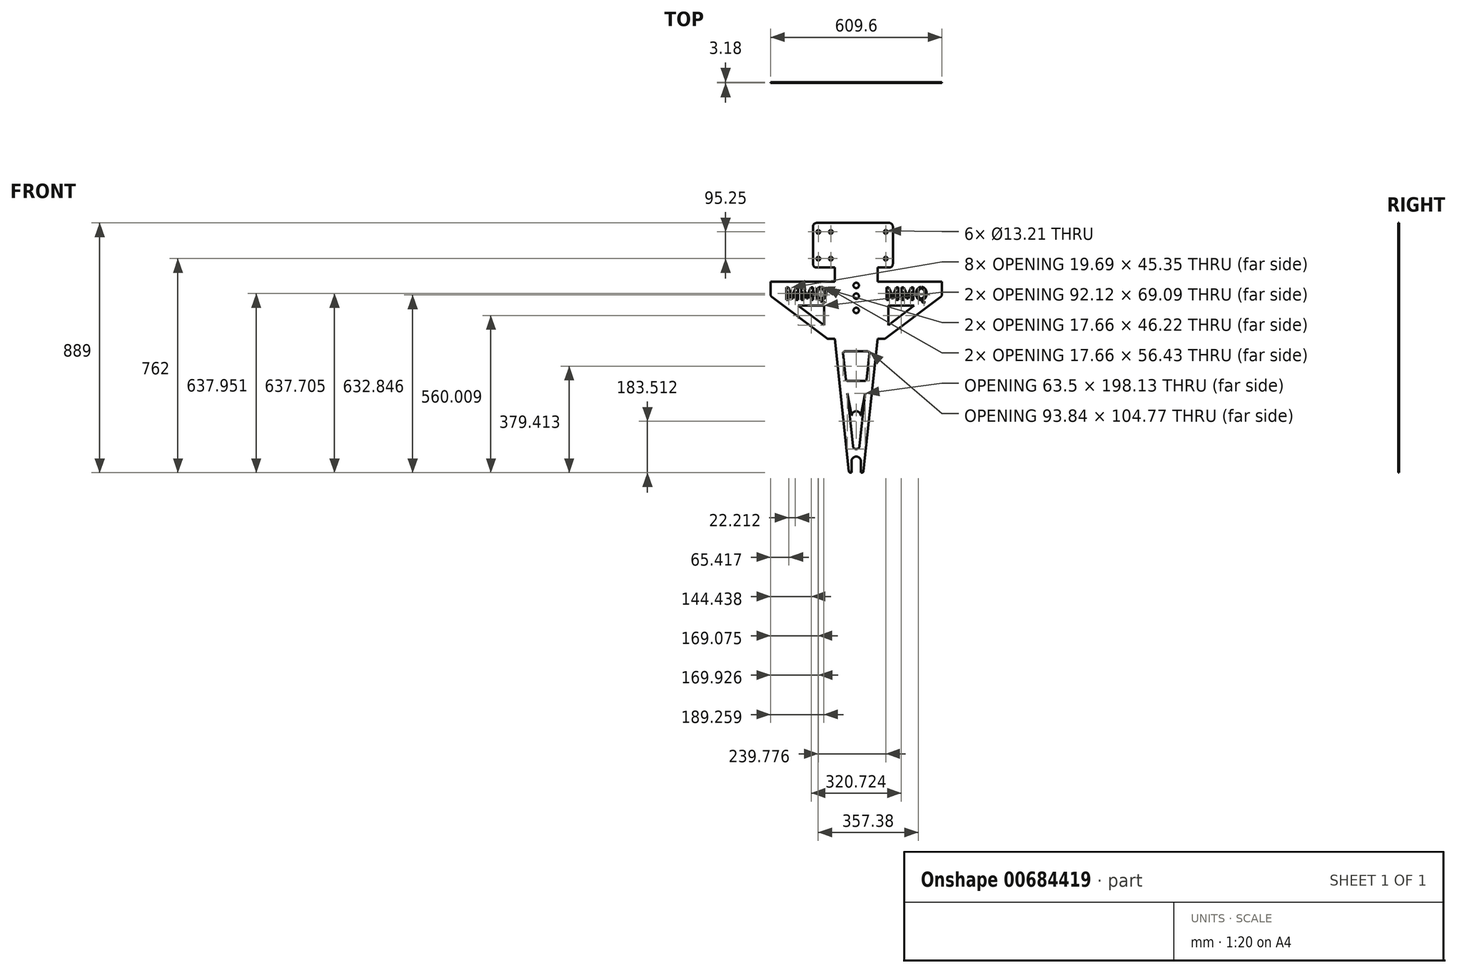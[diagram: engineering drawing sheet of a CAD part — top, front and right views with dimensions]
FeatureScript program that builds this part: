
annotation { "Feature Type Name" : "Feature", "Feature Type Description" : "" }
export const myFeature = defineFeature(function(context is Context, id is Id, definition is map)
    precondition{}
    {
        {
            var Q0;
            Q0=qCreatedBy(makeId("Front.planeOp"),FACE);
            var sketch = newSketch(context, id + "F0", { "sketchPlane" : qUnion([Q0])});
            skLineSegment(sketch, "E0.bottom", {"start": v(-97.37, -101.6) * mm, "end": v(-76.2, -101.6) * mm});
            skLineSegment(sketch, "E0.top", {"start": v(-304.8, 101.6) * mm, "end": v(-76.2, 101.6) * mm});
            skLineSegment(sketch, "E0.left", {"start": v(-304.8, 57.15) * mm, "end": v(-304.8, 101.6) * mm});
            skLineSegment(sketch, "E0.right", {"start": v(304.8, 57.15) * mm, "end": v(304.8, 101.6) * mm});
            skPoint(sketch, "E0.middle", {"position": v(0, 0) * mm});
            skLineSegment(sketch, "E1", {"start": v(-16.52, -577.85) * mm, "end": v(-19.7, -577.85) * mm});
            skLineSegment(sketch, "E2", {"start": v(16.5, -577.85) * mm, "end": v(19.7, -577.85) * mm});
            skPoint(sketch, "E3", {"position": v(-76.2, -101.6) * mm});
            skPoint(sketch, "E4", {"position": v(76.2, -101.6) * mm});
            skLineSegment(sketch, "E5", {"start": v(-76.2, -101.6) * mm, "end": v(-26, -572.17) * mm});
            skLineSegment(sketch, "E6", {"start": v(76.2, -101.6) * mm, "end": v(26, -572.17) * mm});
            skPoint(sketch, "E7", {"position": v(0, -295.28) * mm});
            skPoint(sketch, "E8", {"position": v(0, -523.88) * mm});
            skPoint(sketch, "E9", {"position": v(-31.75, -295.28) * mm});
            skPoint(sketch, "E10", {"position": v(31.75, -295.28) * mm});
            skArc(sketch, "E11", {"start": v(15.88, -374.65) * mm, "mid": v(0, -358.78) * mm, "end": v(-15.87, -374.65) * mm});
            skLineSegment(sketch, "E12", {"start": v(-31.75, -295.28) * mm, "end": v(-16.18, -374.65) * mm});
            skLineSegment(sketch, "E13", {"start": v(31.75, -295.28) * mm, "end": v(16.18, -374.65) * mm});
            skLineSegment(sketch, "E14", {"start": v(-31.75, -295.28) * mm, "end": v(-11.88, -481.52) * mm});
            skLineSegment(sketch, "E15", {"start": v(31.75, -295.28) * mm, "end": v(11.88, -481.52) * mm});
            skArc(sketch, "E16", {"start": v(-11.88, -481.52) * mm, "mid": v(0, -493.4) * mm, "end": v(11.88, -481.52) * mm});
            skLineSegment(sketch, "E17", {"start": v(-76.2, 101.6) * mm, "end": v(-76.2, 152.4) * mm});
            skPoint(sketch, "E17.startSnap0", {"position": v(0, 101.6) * mm});
            skLineSegment(sketch, "E18", {"start": v(76.2, 101.6) * mm, "end": v(76.2, 152.4) * mm});
            skLineSegment(sketch, "E19", {"start": v(-76.2, 152.4) * mm, "end": v(-141.22, 152.4) * mm});
            skLineSegment(sketch, "E20", {"start": v(76.2, 152.4) * mm, "end": v(117.6, 152.4) * mm});
            skPoint(sketch, "E21.orphan", {"position": v(-141.22, 361.95) * mm});
            skPoint(sketch, "E22.orphan", {"position": v(117.6, 361.95) * mm});
            skLineSegment(sketch, "E23", {"start": v(-153.92, 298.45) * mm, "end": v(-153.92, 165.1) * mm});
            skPoint(sketch, "E23.endSnap0", {"position": v(-108.71, 152.4) * mm});
            skLineSegment(sketch, "E24", {"start": v(130.3, 298.45) * mm, "end": v(130.3, 165.1) * mm});
            skLineSegment(sketch, "E25", {"start": v(-141.22, 152.4) * mm, "end": v(-141.22, 152.4) * mm});
            skLineSegment(sketch, "E26", {"start": v(117.6, 152.4) * mm, "end": v(117.6, 152.4) * mm});
            skPoint(sketch, "E27.end.orphan", {"position": v(-141.22, 317.6) * mm});
            skPoint(sketch, "E28.start.orphan", {"position": v(117.6, 317.5) * mm});
            skPoint(sketch, "E29.start.orphan", {"position": v(-15.88, -539.75) * mm});
            skPoint(sketch, "E30.start.orphan", {"position": v(15.87, -539.75) * mm});
            skPoint(sketch, "E31.center.orphan", {"position": v(0, -552.44) * mm});
            skArc(sketch, "E32", {"start": v(16.5, -536.58) * mm, "mid": v(0, -520.07) * mm, "end": v(-16.52, -536.58) * mm});
            skLineSegment(sketch, "E33", {"start": v(16.5, -577.85) * mm, "end": v(16.5, -536.58) * mm});
            skLineSegment(sketch, "E34", {"start": v(-16.52, -577.85) * mm, "end": v(-16.52, -536.58) * mm});
            skPoint(sketch, "E35", {"position": v(0, -520.07) * mm});
            skLineSegment(sketch, "E36", {"start": v(-299.72, 46.99) * mm, "end": v(-104.99, -99.06) * mm});
            skLineSegment(sketch, "E37", {"start": v(299.72, 46.99) * mm, "end": v(104.99, -99.06) * mm});
            skPoint(sketch, "E38.orphan", {"position": v(-304.8, -101.6) * mm});
            skPoint(sketch, "E39.orphan", {"position": v(304.8, -101.6) * mm});
            skLineSegment(sketch, "E40.trimOffspring", {"start": v(76.2, 101.6) * mm, "end": v(304.8, 101.6) * mm});
            skLineSegment(sketch, "E41.trimOffspring", {"start": v(76.2, -101.6) * mm, "end": v(97.37, -101.6) * mm});
            skCircle(sketch, "E42", {"center": v(104.9, 279.4) * mm, "radius": 6.6 * mm});
            skCircle(sketch, "E43", {"center": v(104.9, 184.15) * mm, "radius": 6.6 * mm});
            skCircle(sketch, "E44", {"center": v(-90.42, 184.15) * mm, "radius": 6.6 * mm});
            skCircle(sketch, "E45", {"center": v(-90.42, 279.4) * mm, "radius": 6.6 * mm});
            skPoint(sketch, "E46", {"position": v(0, 184.15) * mm});
            skPoint(sketch, "E47", {"position": v(0, 279.4) * mm});
            skLineSegment(sketch, "E48", {"start": v(-141.22, 311.15) * mm, "end": v(117.6, 311.15) * mm});
            skPoint(sketch, "E49.end.orphan", {"position": v(130.3, 317.5) * mm});
            skPoint(sketch, "E50.orphan", {"position": v(-153.92, 317.6) * mm});
            skLineSegment(sketch, "E51", {"start": v(-115.82, 285.75) * mm, "end": v(-115.82, 177.8) * mm});
            skCircle(sketch, "E52", {"center": v(-134.87, 184.15) * mm, "radius": 6.6 * mm});
            skCircle(sketch, "E53", {"center": v(-134.87, 279.4) * mm, "radius": 6.6 * mm});
            skPoint(sketch, "E54", {"position": v(-115.82, 285.75) * mm});
            skPoint(sketch, "E55", {"position": v(-115.82, 177.8) * mm});
            skPoint(sketch, "E56.orphan", {"position": v(-115.82, 311.15) * mm});
            skPoint(sketch, "E57.orphan", {"position": v(-115.82, 152.4) * mm});
            skPoint(sketch, "E58.orphan", {"position": v(0, -101.6) * mm});
            skPoint(sketch, "E59.trimOffspring.end.orphan", {"position": v(0, -539.75) * mm});
            skCircle(sketch, "E60", {"center": v(0, 50.8) * mm, "radius": 9.78 * mm});
            skText(sketch, "E61", { "text": "MMQ", "fontName": "AllertaStencil-Regular.ttf"});
            skPoint(sketch, "E62.visualSharp", {"position": v(-153.92, 311.15) * mm});
            skArc(sketch, "E62.filletArc", {"start": v(-141.22, 311.15) * mm, "mid": v(-150.2, 307.43) * mm, "end": v(-153.92, 298.45) * mm});
            skPoint(sketch, "E63.visualSharp", {"position": v(-153.92, 152.4) * mm});
            skArc(sketch, "E63.filletArc", {"start": v(-153.92, 165.1) * mm, "mid": v(-150.2, 156.12) * mm, "end": v(-141.22, 152.4) * mm});
            skPoint(sketch, "E64.visualSharp", {"position": v(130.3, 311.15) * mm});
            skArc(sketch, "E64.filletArc", {"start": v(130.3, 298.45) * mm, "mid": v(126.58, 307.43) * mm, "end": v(117.6, 311.15) * mm});
            skPoint(sketch, "E65.visualSharp", {"position": v(130.3, 152.4) * mm});
            skArc(sketch, "E65.filletArc", {"start": v(117.6, 152.4) * mm, "mid": v(126.58, 156.12) * mm, "end": v(130.3, 165.1) * mm});
            skPoint(sketch, "E66.visualSharp", {"position": v(-304.8, 50.8) * mm});
            skArc(sketch, "E66.filletArc", {"start": v(-304.8, 57.15) * mm, "mid": v(-303.46, 51.47) * mm, "end": v(-299.72, 46.99) * mm});
            skPoint(sketch, "E67.visualSharp", {"position": v(-101.6, -101.6) * mm});
            skArc(sketch, "E67.filletArc", {"start": v(-104.99, -99.06) * mm, "mid": v(-101.38, -100.95) * mm, "end": v(-97.37, -101.6) * mm});
            skPoint(sketch, "E68.visualSharp", {"position": v(101.6, -101.6) * mm});
            skArc(sketch, "E68.filletArc", {"start": v(97.37, -101.6) * mm, "mid": v(101.38, -100.95) * mm, "end": v(104.99, -99.06) * mm});
            skPoint(sketch, "E69.visualSharp", {"position": v(304.8, 50.8) * mm});
            skArc(sketch, "E69.filletArc", {"start": v(299.72, 46.99) * mm, "mid": v(303.46, 51.47) * mm, "end": v(304.8, 57.15) * mm});
            skPoint(sketch, "E70.visualSharp", {"position": v(-25.4, -577.85) * mm});
            skArc(sketch, "E70.filletArc", {"start": v(-26, -572.17) * mm, "mid": v(-23.94, -576.22) * mm, "end": v(-19.7, -577.85) * mm});
            skPoint(sketch, "E71.visualSharp", {"position": v(25.4, -577.85) * mm});
            skArc(sketch, "E71.filletArc", {"start": v(19.7, -577.85) * mm, "mid": v(23.94, -576.22) * mm, "end": v(26, -572.17) * mm});
            skLineSegment(sketch, "E72", {"start": v(-37.1, -245.15) * mm, "end": v(-46.92, -153.07) * mm});
            skLineSegment(sketch, "E73", {"start": v(37.1, -245.15) * mm, "end": v(46.92, -153.07) * mm});
            skLineSegment(sketch, "E74", {"start": v(15.2, -146.05) * mm, "end": v(-15.2, -146.05) * mm});
            skLineSegment(sketch, "E75", {"start": v(-30.78, -250.83) * mm, "end": v(30.78, -250.83) * mm});
            skPoint(sketch, "E76.visualSharp", {"position": v(-47.67, -146.05) * mm});
            skArc(sketch, "E76.filletArc", {"start": v(-40.6, -146.05) * mm, "mid": v(-45.33, -148.15) * mm, "end": v(-46.92, -153.07) * mm});
            skPoint(sketch, "E77.visualSharp", {"position": v(47.67, -146.05) * mm});
            skArc(sketch, "E77.filletArc", {"start": v(46.92, -153.07) * mm, "mid": v(45.33, -148.15) * mm, "end": v(40.6, -146.05) * mm});
            skPoint(sketch, "E78.visualSharp", {"position": v(36.5, -250.83) * mm});
            skArc(sketch, "E78.filletArc", {"start": v(30.78, -250.83) * mm, "mid": v(35.03, -249.2) * mm, "end": v(37.1, -245.15) * mm});
            skPoint(sketch, "E79.visualSharp", {"position": v(-36.5, -250.83) * mm});
            skArc(sketch, "E79.filletArc", {"start": v(-37.1, -245.15) * mm, "mid": v(-35.03, -249.2) * mm, "end": v(-30.78, -250.83) * mm});
            skLineSegment(sketch, "E80", {"start": v(-206.42, 16.7) * mm, "end": v(-114.3, 16.7) * mm});
            skLineSegment(sketch, "E81", {"start": v(-114.3, 16.7) * mm, "end": v(-114.3, -52.39) * mm});
            skLineSegment(sketch, "E82", {"start": v(-114.3, -52.39) * mm, "end": v(-206.42, 16.7) * mm});
            skLineSegment(sketch, "E83", {"start": v(114.3, 16.7) * mm, "end": v(114.3, -52.39) * mm});
            skLineSegment(sketch, "E84", {"start": v(114.3, -52.39) * mm, "end": v(206.42, 16.7) * mm});
            skLineSegment(sketch, "E85", {"start": v(206.42, 16.7) * mm, "end": v(114.3, 16.7) * mm});
            skPoint(sketch, "E86.center.orphan", {"position": v(0, 26.68) * mm});
            skCircle(sketch, "E87", {"center": v(0, 0) * mm, "radius": 9.78 * mm});
            skLineSegment(sketch, "E88", {"start": v(-76.2, 76.2) * mm, "end": v(-76.2, 12.7) * mm});
            skPoint(sketch, "E88.startSnap0", {"position": v(-76.2, 127) * mm});
            skPoint(sketch, "E89", {"position": v(-76.2, 0) * mm});
            skPoint(sketch, "E90", {"position": v(-76.2, 12.7) * mm});
            skPoint(sketch, "E91", {"position": v(-76.42, -12.7) * mm});
            skPoint(sketch, "E92.orphan", {"position": v(-76.2, -76.2) * mm});
            skLineSegment(sketch, "E93", {"start": v(-76.42, -12.7) * mm, "end": v(-76.2, -76.2) * mm});
            skLineSegment(sketch, "E94", {"start": v(76.2, -12.7) * mm, "end": v(76.2, -76.2) * mm});
            skLineSegment(sketch, "E95", {"start": v(76.2, 76.2) * mm, "end": v(76.2, 54.09) * mm});
            skLineSegment(sketch, "E96", {"start": v(76.2, 76.2) * mm, "end": v(76.2, 12.7) * mm});
            skPoint(sketch, "E97", {"position": v(-15.2, -146.05) * mm});
            skPoint(sketch, "E98", {"position": v(15.2, -146.05) * mm});
            skPoint(sketch, "E99", {"position": v(-21.76, -307.12) * mm});
            skLineSegment(sketch, "E100", {"start": v(-40.6, -146.05) * mm, "end": v(40.6, -146.05) * mm});
            skPoint(sketch, "E101", {"position": v(-15.87, -295.28) * mm});
            skPoint(sketch, "E102", {"position": v(15.88, -295.28) * mm});
            skLineSegment(sketch, "E103", {"start": v(-15.87, -295.28) * mm, "end": v(15.88, -295.28) * mm});
            skPoint(sketch, "E104.sketch_text.ascent.start.orphan", {"position": v(-254.89, 82.55) * mm});
            skPoint(sketch, "E104.sketch_text.baseline.start.orphan", {"position": v(-254.89, 37.18) * mm});
            skPoint(sketch, "E104.sketch_text.right.end.orphan", {"position": v(-102.49, 82.55) * mm});
            skText(sketch, "E105", { "text": "MMQ", "fontName": "AllertaStencil-Regular.ttf"});
            skLineSegment(sketch, "E106", {"start": v(-15.87, -374.65) * mm, "end": v(-16.18, -374.65) * mm});
            skLineSegment(sketch, "E107", {"start": v(15.88, -374.65) * mm, "end": v(16.18, -374.65) * mm});
            skCircle(sketch, "E108", {"center": v(0, 88.9) * mm, "radius": 9.78 * mm});
            const initialGuessF0  = {"E61": [0.10249, 0.03718, 1, 0, 0.04537], "E105": [-0.25489, 0.03718, 1, 0, 0.04537]};
            skSetInitialGuess(sketch, initialGuessF0);
            skSolve(sketch);
        }
        {
            var Q0;
            Q0=makeQuery(id+"F0.imprint","IMPRINT",FACE,{"disambiguationData":[TD([[makeQuery(id+"F0.imprint","IMPRINT",EDGE,{"derivedFrom":sQuery(id+"F0.wireOp",EDGE,"E0.bottom")}),1.0]])]});
            var Q1;
            Q1=makeQuery(id+"F0.imprint","IMPRINT",FACE,{"disambiguationData":[TD([[makeQuery(id+"F0.imprint","IMPRINT",EDGE,{"derivedFrom":sQuery(id+"F0.wireOp",EDGE,"1f9559ab-6133-495f-9a9a-994a82361416")}),-1.0]])]});
            extrude(context, id + "F1", {"entities" : qUnion([Q0, Q1]), "depth" : 3.17 * mm, "offsetDistance" : 25.4 * mm});
        }
    });
